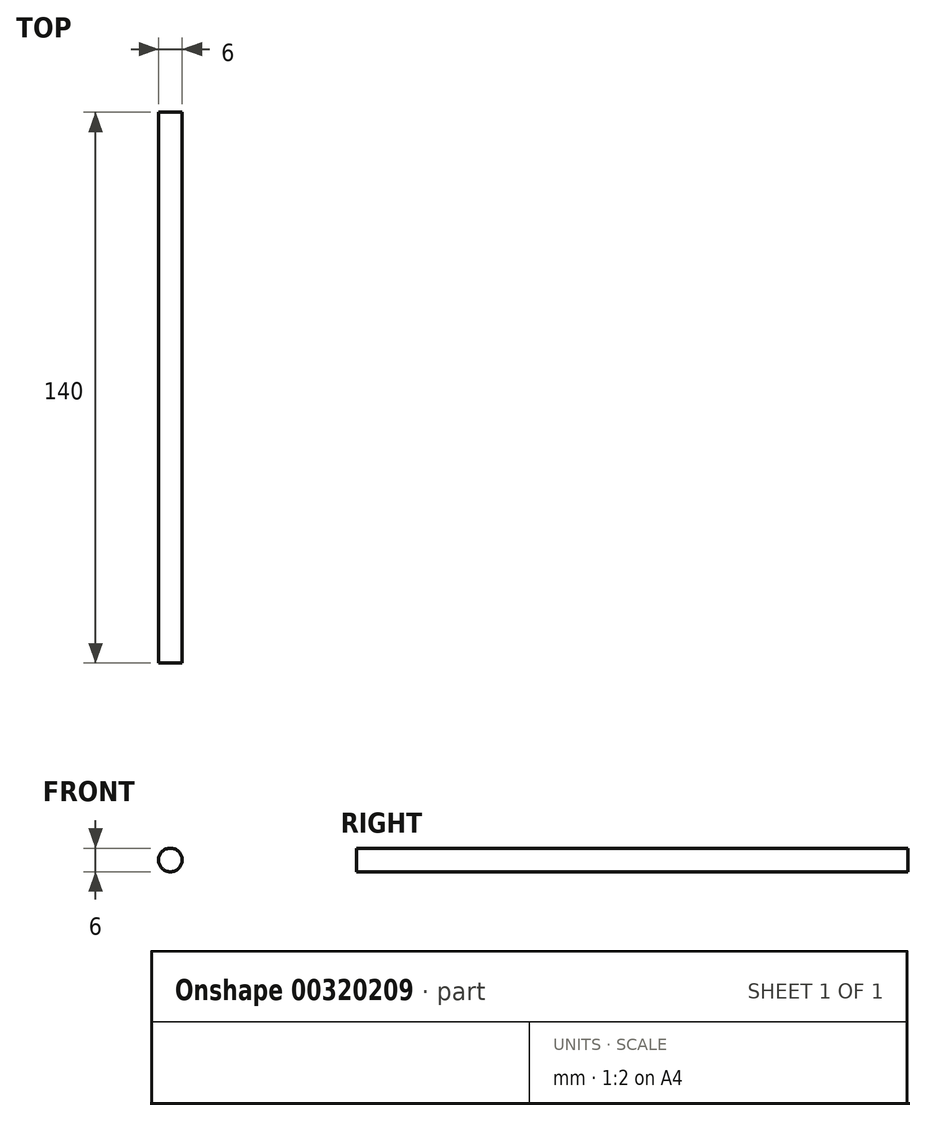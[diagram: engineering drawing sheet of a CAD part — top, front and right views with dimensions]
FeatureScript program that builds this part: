
annotation { "Feature Type Name" : "Feature", "Feature Type Description" : "" }
export const myFeature = defineFeature(function(context is Context, id is Id, definition is map)
    precondition{}
    {
        {
            var Q0;
            Q0=qCreatedBy(makeId("Front.planeOp"),FACE);
            var sketch = newSketch(context, id + "F0", { "sketchPlane" : qUnion([Q0])});
            skCircle(sketch, "E0", {"center": v(0, 0) * mm, "radius": 3 * mm});
            skSolve(sketch);
        }
        {
            var Q0;
            Q0=qSketchRegion(id+"F0",true);
            extrude(context, id + "F1", {"entities" : qUnion([Q0]), "endBound" : BoundingType.SYMMETRIC, "depth" : 140 * mm});
        }
    });
